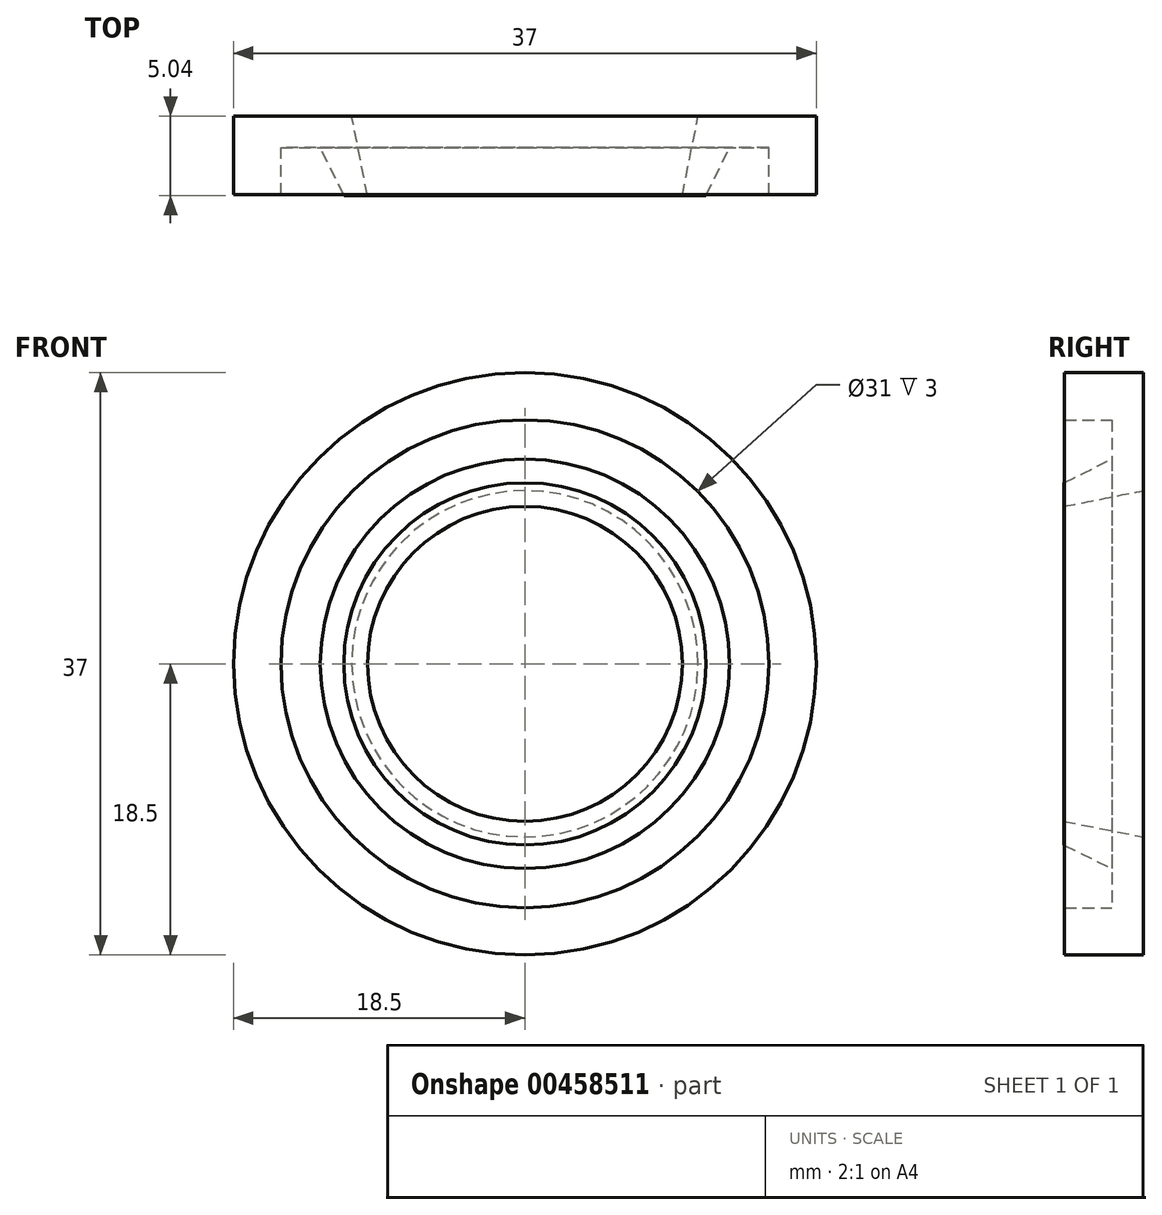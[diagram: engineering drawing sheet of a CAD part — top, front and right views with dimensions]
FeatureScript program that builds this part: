
annotation { "Feature Type Name" : "Feature", "Feature Type Description" : "" }
export const myFeature = defineFeature(function(context is Context, id is Id, definition is map)
    precondition{}
    {
        {
            var Q0;
            Q0=qCreatedBy(makeId("Right.planeOp"),FACE);
            var sketch = newSketch(context, id + "F0", { "sketchPlane" : qUnion([Q0])});
            skLineSegment(sketch, "E0", {"start": v(0, 11) * mm, "end": v(0, 18.5) * mm});
            skLineSegment(sketch, "E1", {"start": v(0, 18.5) * mm, "end": v(-5, 18.5) * mm});
            skLineSegment(sketch, "E2", {"start": v(-5, 18.5) * mm, "end": v(-5, 15.5) * mm});
            skLineSegment(sketch, "E3", {"start": v(-5, 15.5) * mm, "end": v(-2, 15.5) * mm});
            skLineSegment(sketch, "E4", {"start": v(-2, 13) * mm, "end": v(-2, 15.5) * mm});
            skLineSegment(sketch, "E5", {"start": v(-2, 13) * mm, "end": v(-5.04, 11.5) * mm});
            skLineSegment(sketch, "E6", {"start": v(-5.04, 11.5) * mm, "end": v(-5.04, 10) * mm});
            skLineSegment(sketch, "E7", {"start": v(-5.04, 10) * mm, "end": v(0, 11) * mm});
            skLineSegment(sketch, "E8", {"start": v(5.26, 0) * mm, "end": v(-3.6, 0) * mm});
            skSolve(sketch);
        }
        {
            var Q0;
            Q0=makeQuery(id+"F0.imprint","IMPRINT",FACE,{"disambiguationData":[TD([[makeQuery(id+"F0.imprint","IMPRINT",EDGE,{"derivedFrom":sQuery(id+"F0.wireOp",EDGE,"E0")}),1.0]])]});
            var Q1;
            Q1=sQuery(id+"F0.wireOp",EDGE,"E8");
            revolve(context, id + "F1", {"entities" : qUnion([Q0]), "axis" : qUnion([Q1]), "revolveType" : RevolveType.FULL});
        }
    });
